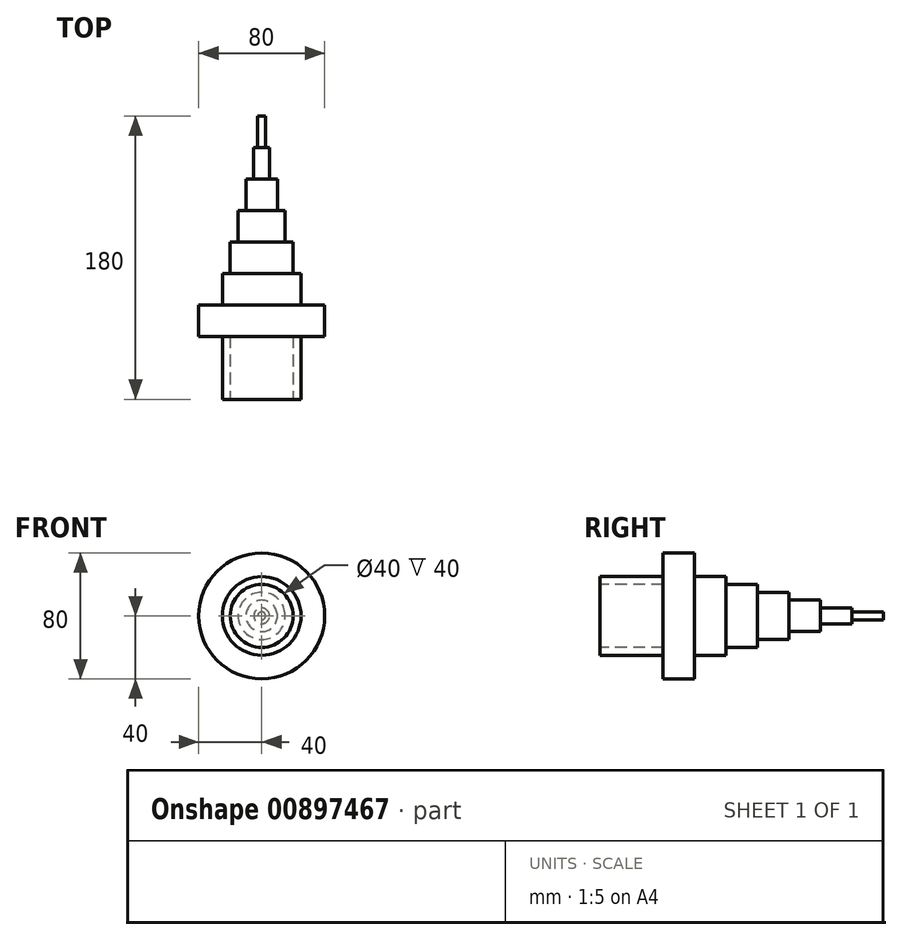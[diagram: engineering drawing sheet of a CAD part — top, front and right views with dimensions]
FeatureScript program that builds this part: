
annotation { "Feature Type Name" : "Feature", "Feature Type Description" : "" }
export const myFeature = defineFeature(function(context is Context, id is Id, definition is map)
    precondition{}
    {
        {
            var Q0;
            Q0=qCreatedBy(makeId("Front.planeOp"),FACE);
            var sketch = newSketch(context, id + "F0", { "sketchPlane" : qUnion([Q0])});
            skCircle(sketch, "E0", {"center": v(0, 0) * mm, "radius": 20 * mm});
            skSolve(sketch);
        }
        {
            var Q0;
            Q0 = qSketchRegion(id + "F0", true);
            extrude(context, id + "F1", {"entities" : qUnion([Q0]), "depth" : 20 * mm, "offsetDistance" : 25.4 * mm});
        }
        {
            var Q0;
            Q0=makeQuery(id+"F1.opExtrude","CAP_FACE",FACE,{"disambiguationData":[OSD([sQuery(id+"F0.wireOp",EDGE,"E0")])],"isStart":true});
            var sketch = newSketch(context, id + "F2", { "sketchPlane" : qUnion([Q0])});
            skCircle(sketch, "E1", {"center": v(0, 0) * mm, "radius": 15 * mm});
            skSolve(sketch);
        }
        {
            var Q0;
            Q0 = qSketchRegion(id + "F2", true);
            extrude(context, id + "F3", {"entities" : qUnion([Q0]), "operationType" : NewBodyOperationType.ADD, "depth" : 20 * mm, "offsetDistance" : 25.4 * mm});
        }
        {
            var Q0;
            Q0=makeQuery(id+"F1.opExtrude","CAP_FACE",FACE,{"disambiguationData":[OSD([sQuery(id+"F0.wireOp",EDGE,"E0")])],"isStart":false});
            var sketch = newSketch(context, id + "F4", { "sketchPlane" : qUnion([Q0])});
            skCircle(sketch, "E2", {"center": v(0, 0) * mm, "radius": 25 * mm});
            skSolve(sketch);
        }
        {
            var Q0;
            Q0 = qSketchRegion(id + "F4", true);
            extrude(context, id + "F5", {"entities" : qUnion([Q0]), "operationType" : NewBodyOperationType.ADD, "depth" : 20 * mm, "offsetDistance" : 25.4 * mm});
        }
        {
            var Q0;
            Q0=makeQuery(id+"F5.opExtrude","CAP_FACE",FACE,{"disambiguationData":[OSD([sQuery(id+"F4.wireOp",EDGE,"E2")])],"isStart":false});
            var sketch = newSketch(context, id + "F6", { "sketchPlane" : qUnion([Q0])});
            skCircle(sketch, "E3", {"center": v(0, 0) * mm, "radius": 40 * mm});
            skSolve(sketch);
        }
        {
            var Q0;
            Q0 = qSketchRegion(id + "F6", true);
            extrude(context, id + "F7", {"entities" : qUnion([Q0]), "operationType" : NewBodyOperationType.ADD, "depth" : 20 * mm, "offsetDistance" : 25.4 * mm});
        }
        {
            var Q0;
            Q0=makeQuery(id+"F7.opExtrude","CAP_FACE",FACE,{"disambiguationData":[OSD([sQuery(id+"F6.wireOp",EDGE,"E3")])],"isStart":false});
            var sketch = newSketch(context, id + "F8", { "sketchPlane" : qUnion([Q0])});
            skCircle(sketch, "E4", {"center": v(0, 0) * mm, "radius": 25 * mm});
            skSolve(sketch);
        }
        {
            var Q0;
            Q0 = qSketchRegion(id + "F8", true);
            extrude(context, id + "F9", {"entities" : qUnion([Q0]), "operationType" : NewBodyOperationType.ADD, "depth" : 40 * mm, "offsetDistance" : 25.4 * mm});
        }
        {
            var Q0;
            Q0=makeQuery(id+"F9.opExtrude","CAP_FACE",FACE,{"disambiguationData":[OSD([sQuery(id+"F8.wireOp",EDGE,"E4")])],"isStart":false});
            var sketch = newSketch(context, id + "F10", { "sketchPlane" : qUnion([Q0])});
            skCircle(sketch, "E5", {"center": v(0, 0) * mm, "radius": 20 * mm});
            skSolve(sketch);
        }
        {
            var Q0;
            Q0 = qSketchRegion(id + "F10", true);
            extrude(context, id + "F11", {"entities" : qUnion([Q0]), "operationType" : NewBodyOperationType.REMOVE, "oppositeDirection" : true, "depth" : 40 * mm, "offsetDistance" : 25.4 * mm});
        }
        {
            var Q0;
            Q0=makeQuery(id+"F3.opExtrude","CAP_FACE",FACE,{"disambiguationData":[OSD([sQuery(id+"F2.wireOp",EDGE,"E1")])],"isStart":false});
            var sketch = newSketch(context, id + "F12", { "sketchPlane" : qUnion([Q0])});
            skCircle(sketch, "E6", {"center": v(0, 0) * mm, "radius": 10 * mm});
            skSolve(sketch);
        }
        {
            var Q0;
            Q0 = qSketchRegion(id + "F12", true);
            extrude(context, id + "F13", {"entities" : qUnion([Q0]), "operationType" : NewBodyOperationType.ADD, "depth" : 20 * mm, "offsetDistance" : 25.4 * mm});
        }
        {
            var Q0;
            Q0=makeQuery(id+"F13.opExtrude","CAP_FACE",FACE,{"disambiguationData":[OSD([sQuery(id+"F12.wireOp",EDGE,"E6")])],"isStart":false});
            var sketch = newSketch(context, id + "F14", { "sketchPlane" : qUnion([Q0])});
            skCircle(sketch, "E7", {"center": v(0, 0) * mm, "radius": 5 * mm});
            skSolve(sketch);
        }
        {
            var Q0;
            Q0 = qSketchRegion(id + "F14", true);
            extrude(context, id + "F15", {"entities" : qUnion([Q0]), "operationType" : NewBodyOperationType.ADD, "depth" : 20 * mm, "offsetDistance" : 25.4 * mm});
        }
        {
            var Q0;
            Q0=makeQuery(id+"F15.opExtrude","CAP_FACE",FACE,{"disambiguationData":[OSD([sQuery(id+"F14.wireOp",EDGE,"E7")])],"isStart":false});
            var sketch = newSketch(context, id + "F16", { "sketchPlane" : qUnion([Q0])});
            skCircle(sketch, "E8", {"center": v(0, 0) * mm, "radius": 2.5 * mm});
            skSolve(sketch);
        }
        {
            var Q0;
            Q0 = qSketchRegion(id + "F16", true);
            extrude(context, id + "F17", {"entities" : qUnion([Q0]), "operationType" : NewBodyOperationType.ADD, "depth" : 20 * mm, "offsetDistance" : 25.4 * mm});
        }
    });
